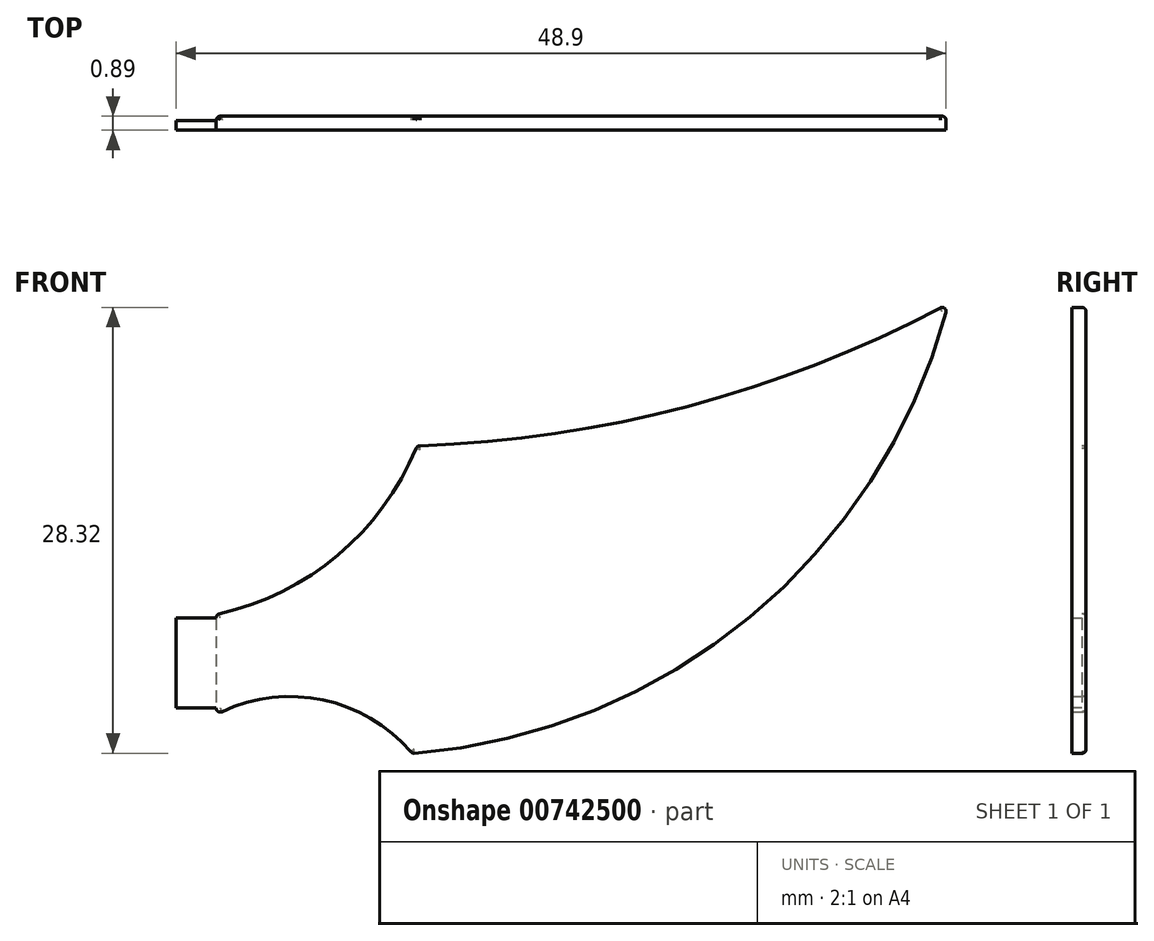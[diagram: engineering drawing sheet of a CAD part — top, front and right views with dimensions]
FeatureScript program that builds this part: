
annotation { "Feature Type Name" : "Feature", "Feature Type Description" : "" }
export const myFeature = defineFeature(function(context is Context, id is Id, definition is map)
    precondition{}
    {
        {
            var Q0;
            Q0=qCreatedBy(makeId("Front.planeOp"),FACE);
            var sketch = newSketch(context, id + "F0", { "sketchPlane" : qUnion([Q0])});
            skLineSegment(sketch, "E0", {"start": v(0, 0) * mm, "end": v(0, 6.35) * mm});
            skLineSegment(sketch, "E1", {"start": v(0, 6.35) * mm, "end": v(12.77, 17.06) * mm, "construction": true});
            skLineSegment(sketch, "E2", {"start": v(12.77, 17.06) * mm, "end": v(46.5, 26.1) * mm, "construction": true});
            skLineSegment(sketch, "E3", {"start": v(12.77, 17.06) * mm, "end": v(12.77, 6.6) * mm, "construction": true});
            skLineSegment(sketch, "E4", {"start": v(46.5, 26.1) * mm, "end": v(12.45, -2.47) * mm, "construction": true});
            skLineSegment(sketch, "E5", {"start": v(46.5, 26.1) * mm, "end": v(46.5, 12.28) * mm, "construction": true});
            skLineSegment(sketch, "E6", {"start": v(0, 0) * mm, "end": v(12.45, -2.47) * mm, "construction": true});
            skArc(sketch, "E7", {"start": v(0, 6.35) * mm, "mid": v(7.72, 10.12) * mm, "end": v(12.77, 17.06) * mm});
            skArc(sketch, "E8", {"start": v(12.77, 17.06) * mm, "mid": v(30.16, 19.63) * mm, "end": v(46.5, 26.1) * mm});
            skArc(sketch, "E9", {"start": v(12.45, -2.47) * mm, "mid": v(34.08, 6.34) * mm, "end": v(46.5, 26.1) * mm});
            skArc(sketch, "E10", {"start": v(12.45, -2.47) * mm, "mid": v(6.66, 0.95) * mm, "end": v(0, 0) * mm});
            skSolve(sketch);
        }
        {
            var Q0;
            Q0=makeQuery(id+"F0.imprint","IMPRINT",FACE,{"disambiguationData":[TD([[makeQuery(id+"F0.imprint","IMPRINT",EDGE,{"derivedFrom":sQuery(id+"F0.wireOp",EDGE,"E0")}),-1.0]])]});
            extrude(context, id + "F1", {"entities" : qUnion([Q0]), "depth" : 1.59 * mm, "offsetDistance" : 25.4 * mm});
        }
        {
            var Q0;
            Q0=makeQuery(id+"F1.opExtrude","CAP_EDGE",EDGE,{"disambiguationData":[OSD([sQuery(id+"F0.wireOp",EDGE,"E7")])],"isStart":true});
            var Q1;
            Q1=makeQuery(id+"F1.opExtrude","CAP_EDGE",EDGE,{"disambiguationData":[OSD([sQuery(id+"F0.wireOp",EDGE,"E7")])],"isStart":false});
            var Q2;
            Q2=makeQuery(id+"F1.opExtrude","CAP_FACE",FACE,{"disambiguationData":[OSD([sQuery(id+"F0.wireOp",EDGE,"E0"),sQuery(id+"F0.wireOp",EDGE,"E7"),sQuery(id+"F0.wireOp",EDGE,"E8"),sQuery(id+"F0.wireOp",EDGE,"E9"),sQuery(id+"F0.wireOp",EDGE,"E10")])],"isStart":true});
            var Q3;
            Q3=makeQuery(id+"F1.opExtrude","CAP_FACE",FACE,{"disambiguationData":[OSD([sQuery(id+"F0.wireOp",EDGE,"E0"),sQuery(id+"F0.wireOp",EDGE,"E7"),sQuery(id+"F0.wireOp",EDGE,"E8"),sQuery(id+"F0.wireOp",EDGE,"E9"),sQuery(id+"F0.wireOp",EDGE,"E10")])],"isStart":false});
            fillet(context, id + "F2", {"entities" : qUnion([Q0, Q1, Q2, Q3]), "radius" : 0.25 * mm, "tangentPropagation" : true, "allowEdgeOverflow" : false});
        }
        {
            var Q0;
            Q0=makeQuery(id+"F1.opExtrude","SWEPT_EDGE",EDGE,{"disambiguationData":[OSD([sQuery(id+"F0.wireOp",EDGE,"E0"),sQuery(id+"F0.wireOp",EDGE,"E7")])]});
            var Q1;
            Q1=makeQuery(id+"F1.opExtrude","SWEPT_EDGE",EDGE,{"disambiguationData":[OSD([sQuery(id+"F0.wireOp",EDGE,"E0"),sQuery(id+"F0.wireOp",EDGE,"E10")])]});
            var Q2;
            Q2=makeQuery(id+"F1.opExtrude","SWEPT_EDGE",EDGE,{"disambiguationData":[OSD([sQuery(id+"F0.wireOp",EDGE,"E9"),sQuery(id+"F0.wireOp",EDGE,"E10")])]});
            var Q3;
            Q3=makeQuery(id+"F1.opExtrude","SWEPT_EDGE",EDGE,{"disambiguationData":[OSD([sQuery(id+"F0.wireOp",EDGE,"E7"),sQuery(id+"F0.wireOp",EDGE,"E8")])]});
            var Q4;
            Q4=makeQuery(id+"F1.opExtrude","SWEPT_EDGE",EDGE,{"disambiguationData":[OSD([sQuery(id+"F0.wireOp",EDGE,"E8"),sQuery(id+"F0.wireOp",EDGE,"E9")])]});
            fillet(context, id + "F3", {"entities" : qUnion([Q0, Q1, Q2, Q3, Q4]), "radius" : 0.25 * mm, "tangentPropagation" : true, "allowEdgeOverflow" : false});
        }
        {
            var Q0;
            Q0=makeQuery(id+"F1.opExtrude","SWEPT_FACE",FACE,{"disambiguationData":[OSD([sQuery(id+"F0.wireOp",EDGE,"E0")])]});
            var sketch = newSketch(context, id + "F4", { "sketchPlane" : qUnion([Q0])});
            skLineSegment(sketch, "E11.bottom", {"start": v(0.25, 6.15) * mm, "end": v(1.33, 6.15) * mm});
            skLineSegment(sketch, "E11.top", {"start": v(0.25, 0.4) * mm, "end": v(1.33, 0.4) * mm});
            skLineSegment(sketch, "E11.left", {"start": v(0.25, 6.15) * mm, "end": v(0.25, 0.4) * mm});
            skLineSegment(sketch, "E11.right", {"start": v(1.33, 6.15) * mm, "end": v(1.33, 0.4) * mm});
            skLineSegment(sketch, "E12.0", {"start": v(0.28, 6.12) * mm, "end": v(0.28, 0.43) * mm});
            skLineSegment(sketch, "E12.1", {"start": v(1.3, 6.12) * mm, "end": v(0.28, 6.12) * mm});
            skLineSegment(sketch, "E12.2", {"start": v(1.3, 0.43) * mm, "end": v(1.3, 6.12) * mm});
            skLineSegment(sketch, "E12.3", {"start": v(0.28, 0.43) * mm, "end": v(1.3, 0.43) * mm});
            skSolve(sketch);
        }
        {
            var Q0;
            Q0=makeQuery(id+"F4.imprint","IMPRINT",FACE,{"disambiguationData":[TD([[makeQuery(id+"F4.imprint","IMPRINT",EDGE,{"derivedFrom":sQuery(id+"F4.wireOp",EDGE,"E12.0")}),1.0]])]});
            extrude(context, id + "F5", {"entities" : qUnion([Q0]), "operationType" : NewBodyOperationType.ADD, "depth" : 2.54 * mm, "offsetDistance" : 25.4 * mm});
        }
        {
            var Q0;
            Q0=qCreatedBy(makeId("Front.planeOp"),FACE);
            cPlane(context, id + "F6", {"entities" : qUnion([Q0]), "cplaneType" : CPlaneType.OFFSET, "offset" : 0.89 * mm, "width" : 152.4 * mm, "height" : 152.4 * mm});
        }
        {
            var Q0;
            Q0=qCreatedBy(id+"F6.planeOp",FACE);
            var sketch = newSketch(context, id + "F7", { "sketchPlane" : qUnion([Q0])});
            skLineSegment(sketch, "E13.bottom", {"start": v(-4.43, -8.7) * mm, "end": v(49.93, -8.7) * mm});
            skLineSegment(sketch, "E13.top", {"start": v(-4.43, 33.74) * mm, "end": v(49.93, 33.74) * mm});
            skLineSegment(sketch, "E13.left", {"start": v(-4.43, -8.7) * mm, "end": v(-4.43, 33.74) * mm});
            skLineSegment(sketch, "E13.right", {"start": v(49.93, -8.7) * mm, "end": v(49.93, 33.74) * mm});
            skSolve(sketch);
        }
        {
            var Q0;
            Q0=makeQuery(id+"F7.imprint","IMPRINT",FACE,{"disambiguationData":[TD([[makeQuery(id+"F7.imprint","IMPRINT",EDGE,{"derivedFrom":sQuery(id+"F7.wireOp",EDGE,"E13.bottom")}),1.0]])]});
            extrude(context, id + "F8", {"entities" : qUnion([Q0]), "operationType" : NewBodyOperationType.REMOVE, "depth" : 10.67 * mm, "offsetDistance" : 25.4 * mm});
        }
    });
